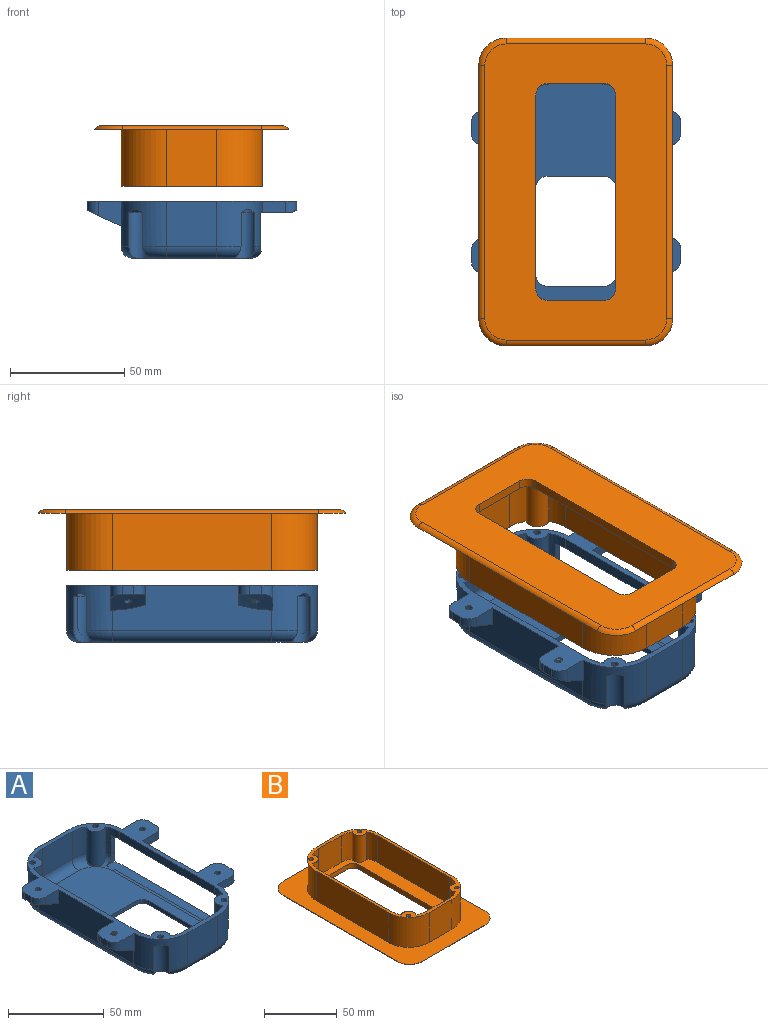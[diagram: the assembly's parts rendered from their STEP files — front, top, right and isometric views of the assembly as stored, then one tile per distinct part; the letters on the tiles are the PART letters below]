
ASSEMBLY  parts=2 mates=1
PART A: 110 faces, bbox 92.7x114x26.4 mm
  f0: cylinder r=20mm len=20mm, axis (0,0,1), area 413.3mm2, adj f12,f23,f36,f37,f71,f72,f96,f101
  f1: cylinder r=20mm len=20mm, axis (0,0,-1), area 421.8mm2, adj f6,f21,f36,f38,f75,f76,f93,f103
  f2: cylinder r=17.5mm len=17.5mm, axis (0,0,-1), area 84.8mm2, adj f4,f18,f36,f66,f103,f104
  f3: plane 40.6x4.89mm, normal (1,0,0), area 198.5mm2, adj f7,f11,f36,f103
  f4: plane 70x4.89mm, normal (-1,0,0), area 342.3mm2, adj f2,f5,f36,f103
  f5: cylinder r=17.5mm len=17.5mm, axis (0,0,1), area 84.8mm2, adj f4,f20,f36,f64,f101,f102,f103,f106
  f6: plane 10x4.89mm, normal (0,-1,0), area 48.9mm2, adj f1,f9,f36,f103
  f7: plane 10x4.89mm, normal (0,1,0), area 48.9mm2, adj f3,f8,f36,f103
  f8: cylinder r=5mm len=5mm, axis (0,0,-1), area 36.4mm2, adj f7,f16,f36,f45,f103
  f9: cylinder r=5mm len=5mm, axis (0,0,1), area 36.4mm2, adj f6,f16,f36,f45,f103
  f10: cylinder r=1.5mm len=4.89mm, axis (0,0,1), area 46.1mm2, adj f36,f103
  f11: plane 10x4.89mm, normal (0,-1,0), area 48.9mm2, adj f3,f14,f36,f103
  f12: plane 10.03x4.91mm, normal (0,1,0), area 48.9mm2, adj f0,f13,f36,f103
  f13: cylinder r=5mm len=5mm, axis (0,0,-1), area 36.4mm2, adj f12,f17,f36,f46,f103
  f14: cylinder r=5mm len=5mm, axis (0,0,1), area 36.4mm2, adj f11,f17,f36,f46,f103
  f15: cylinder r=1.5mm len=4.89mm, axis (0,0,1), area 46.1mm2, adj f36,f103
  f16: plane 13.28x2.33mm, normal (0.42,0,-0.91), area 22.1mm2, adj f8,f9,f45,f103
  f17: plane 13.28x2.33mm, normal (0.42,0,-0.91), area 22.1mm2, adj f13,f14,f46,f103
  f18: torus R=12.5mm, axis (0,0,1), area 28.9mm2, adj f2,f19,f30,f66,f104,f105
  f19: cylinder r=5mm len=70mm, axis (0,-1,0), area 107.7mm2, adj f18,f20,f30,f105
  f20: torus R=12.5mm, axis (0,0,1), area 28.8mm2, adj f5,f19,f30,f64,f105,f106
  f21: torus R=15mm, axis (0,0,1), area 68.5mm2, adj f1,f22,f31,f76,f104,f105
  f22: cylinder r=5mm len=70mm, axis (0,1,0), area 385.2mm2, adj f21,f23,f31,f105
  f23: torus R=15mm, axis (0,0,1), area 68mm2, adj f0,f22,f31,f72,f105,f106
  f24: cylinder r=20mm len=20mm, axis (0,0,1), area 492.1mm2, adj f35,f36,f38,f56,f62,f73,f74,f88
  f25: cylinder r=20mm len=20mm, axis (0,0,-1), area 491.2mm2, adj f35,f36,f37,f49,f61,f77,f78,f90
  f26: cylinder r=1.5mm len=3.37mm, axis (0,0,1), area 30.7mm2, adj f36,f77
  f27: cylinder r=1.5mm len=3.23mm, axis (0,0,1), area 29.7mm2, adj f36,f75
  f28: cylinder r=1.5mm len=3.21mm, axis (0,0,1), area 29.7mm2, adj f36,f73
  f29: cylinder r=1.5mm len=3.35mm, axis (0,0,1), area 31mm2, adj f36,f71
  f30: plane 95x47mm, normal (0,0,1), area 2659mm2, adj f18,f19,f20,f67,f68,f69,f70,f79
  f31: plane 100x52mm, normal (0,0,-1), area 3304.1mm2, adj f21,f22,f23,f67,f68,f69,f70,f72
  f32: cylinder r=17.5mm len=17.5mm, axis (0,0,1), area 152.7mm2, adj f36,f41,f65,f79
  f33: cylinder r=17.5mm len=17.5mm, axis (0,0,1), area 152.7mm2, adj f36,f39,f64,f87
  f34: cylinder r=17.5mm len=17.5mm, axis (0,0,-1), area 152.7mm2, adj f36,f40,f63,f84
  f35: plane 70x20mm, normal (-1,0,0), area 1103.1mm2, adj f24,f25,f36,f47,f54,f61,f62,f89
  f36: plane 110.24x92.04mm, normal (0,0,1), area 1695.1mm2, adj f0,f1,f2,f3,f4,f5,f6,f7
  f37: plane 22x20mm, normal (0,1,0), area 440mm2, adj f0,f25,f36,f95
  f38: plane 22x20mm, normal (0,-1,0), area 440mm2, adj f1,f24,f36,f92
  f39: plane 22x17.5mm, normal (0,-1,0), area 385mm2, adj f33,f36,f42,f86
  f40: plane 70x17.5mm, normal (1,0,0), area 1225mm2, adj f34,f36,f43,f83
  f41: plane 22x17.5mm, normal (0,1,0), area 385mm2, adj f32,f36,f44,f80
  f42: cylinder r=17.5mm len=17.5mm, axis (0,0,-1), area 152.7mm2, adj f36,f39,f63,f85
  f43: cylinder r=17.5mm len=17.5mm, axis (0,0,1), area 152.7mm2, adj f36,f40,f65,f82
  f44: cylinder r=17.5mm len=17.5mm, axis (0,0,-1), area 152.7mm2, adj f36,f41,f66,f81
  f45: plane 5x4mm, normal (1,0,0), area 20mm2, adj f8,f9,f16,f36
  f46: plane 5x4mm, normal (1,0,0), area 20mm2, adj f13,f14,f17,f36
  f47: plane 9.8x8.83mm, normal (0,-1,0), area 67.6mm2, adj f35,f36,f51,f61
  f48: plane 9.87x2.64mm, normal (0,0,-1), area 7.2mm2, adj f50,f51,f52,f61
  f49: plane 11.05x9.86mm, normal (0,1,0), area 85.5mm2, adj f25,f36,f52,f61
  f50: plane 5x4mm, normal (-1,0,0), area 20mm2, adj f36,f48,f51,f52
  f51: cylinder r=5mm len=5mm, axis (0,0,-1), area 32.5mm2, adj f36,f47,f48,f50,f61
  f52: cylinder r=5mm len=6.42mm, axis (0,0,1), area 38.6mm2, adj f36,f48,f49,f50,f61
  f53: cylinder r=1.5mm len=7.61mm, axis (0,0,1), area 66.6mm2, adj f36,f61
  f54: plane 9.8x8.78mm, normal (0,1,0), area 67.1mm2, adj f35,f36,f59,f62
  f55: plane 10.04x2.75mm, normal (0,0,-1), area 7.8mm2, adj f57,f58,f59,f62
  f56: plane 11.03x9.84mm, normal (0,-1,0), area 85.4mm2, adj f24,f36,f58,f62
  f57: plane 5x4mm, normal (-1,0,0), area 20mm2, adj f36,f55,f58,f59
  f58: cylinder r=5mm len=6.43mm, axis (0,0,-1), area 38.6mm2, adj f36,f55,f56,f57,f62
  f59: cylinder r=5mm len=5mm, axis (0,0,1), area 32.4mm2, adj f36,f54,f55,f57,f62
  f60: cylinder r=1.5mm len=7.87mm, axis (0,0,1), area 36.8mm2, adj f36,f62,f107,f108,f109
  f61: cone r=20mm half-angle=65deg, axis (0,0,1), area 217.3mm2, adj f25,f35,f47,f48,f49,f51,f52,f53
  f62: cone r=20mm half-angle=65deg, axis (0,0,1), area 215.7mm2, adj f24,f35,f54,f55,f56,f58,f59,f60
  f63: cylinder r=5mm len=22.5mm, axis (0,0,-1), area 285.5mm2, adj f34,f36,f42,f84,f85
  f64: cylinder r=5mm len=22.5mm, axis (0,0,-1), area 285.5mm2, adj f5,f20,f33,f36,f87
  f65: cylinder r=5mm len=22.5mm, axis (0,0,-1), area 285.5mm2, adj f32,f36,f43,f79,f82
  f66: cylinder r=5mm len=22.5mm, axis (0,0,-1), area 285.5mm2, adj f2,f18,f36,f44,f81
  f67: plane 25.14x2.5mm, normal (0,1,0), area 62.8mm2, adj f30,f31,f97,f100
  f68: plane 38.19x2.5mm, normal (1,0,0), area 95.5mm2, adj f30,f31,f97,f98
  f69: plane 25.14x2.5mm, normal (0,-1,0), area 62.8mm2, adj f30,f31,f98,f99
  f70: plane 38.19x2.5mm, normal (-1,0,0), area 95.5mm2, adj f30,f31,f99,f100
  f71: cone r=0mm half-angle=59deg, axis (0,0,-1), area 48.6mm2, adj f0,f29,f72
  f72: cylinder r=4.5mm len=20mm, axis (0,0,-1), area 332.2mm2, adj f0,f23,f31,f71,f96
  f73: cone r=0mm half-angle=59deg, axis (0,0,-1), area 51.3mm2, adj f24,f28,f74
  f74: cylinder r=4.5mm len=20mm, axis (0,0,-1), area 329.3mm2, adj f24,f31,f73,f88,f91
  f75: cone r=0mm half-angle=59deg, axis (0,0,-1), area 50.2mm2, adj f1,f27,f76
  f76: cylinder r=4.5mm len=20mm, axis (0,0,-1), area 327.8mm2, adj f1,f21,f31,f75,f93
  f77: cone r=0mm half-angle=59deg, axis (0,0,-1), area 49.4mm2, adj f25,f26,f78
  f78: cylinder r=4.5mm len=20mm, axis (0,0,-1), area 333.2mm2, adj f25,f31,f77,f90,f94
  f79: torus R=12.5mm, axis (0,0,1), area 64.5mm2, adj f30,f32,f65,f80
  f80: cylinder r=5mm len=22mm, axis (-1,0,0), area 172.8mm2, adj f30,f41,f79,f81
  f81: torus R=12.5mm, axis (0,0,1), area 64.5mm2, adj f30,f44,f66,f80
  f82: torus R=12.5mm, axis (0,0,1), area 64.5mm2, adj f30,f43,f65,f83
  f83: cylinder r=5mm len=70mm, axis (0,1,0), area 549.8mm2, adj f30,f40,f82,f84
  f84: torus R=12.5mm, axis (0,0,1), area 64.5mm2, adj f30,f34,f63,f83
  f85: torus R=12.5mm, axis (0,0,1), area 64.5mm2, adj f30,f42,f63,f86
  f86: cylinder r=5mm len=22mm, axis (1,0,0), area 172.8mm2, adj f30,f39,f85,f87
  f87: torus R=12.5mm, axis (0,0,1), area 64.5mm2, adj f30,f33,f64,f86
  f88: torus R=15mm, axis (0,0,1), area 81.5mm2, adj f24,f31,f74,f89
  f89: cylinder r=5mm len=70mm, axis (0,-1,0), area 549.8mm2, adj f31,f35,f88,f90
  f90: torus R=15mm, axis (0,0,1), area 80.9mm2, adj f25,f31,f78,f89
  f91: torus R=15mm, axis (0,0,1), area 76mm2, adj f24,f31,f74,f92
  f92: cylinder r=5mm len=22mm, axis (1,0,0), area 172.8mm2, adj f31,f38,f91,f93
  f93: torus R=15mm, axis (0,0,1), area 76.3mm2, adj f1,f31,f76,f92
  f94: torus R=15mm, axis (0,0,1), area 76.5mm2, adj f25,f31,f78,f95
  f95: cylinder r=5mm len=22mm, axis (-1,0,0), area 172.8mm2, adj f31,f37,f94,f96
  f96: torus R=15mm, axis (0,0,1), area 76.7mm2, adj f0,f31,f72,f95
  f97: cylinder r=5mm len=5mm, axis (0,0,1), area 19.6mm2, adj f30,f31,f67,f68
  f98: cylinder r=5mm len=5mm, axis (0,0,1), area 19.6mm2, adj f30,f31,f68,f69
  f99: cylinder r=5mm len=5mm, axis (0,0,-1), area 19.6mm2, adj f30,f31,f69,f70
  f100: cylinder r=5mm len=5mm, axis (0,0,-1), area 19.6mm2, adj f30,f31,f67,f70
  f101: plane 2.61x0.01mm, normal (0,0,-1), area 0mm2, adj f0,f5,f102,f106
  f102: plane 11.98x2.61mm, normal (0,-1,0), area 31.2mm2, adj f0,f5,f101,f103
  f103: plane 80.61x16.42mm, normal (0,0,-1), area 576.3mm2, adj f0,f1,f2,f3,f4,f5,f6,f7
  f104: plane 18.08x7.02mm, normal (0,1,0), area 49.6mm2, adj f1,f2,f18,f21,f103,f105
  f105: plane 80.62x6.49mm, normal (0,0,1), area 439.9mm2, adj f18,f19,f20,f21,f22,f23,f104,f106
  f106: plane 7.02x6.1mm, normal (0,-1,0), area 18.3mm2, adj f0,f5,f20,f23,f101,f105
  f107: plane 0.92x0.61mm, normal (0,1,0), area 0.3mm2, adj f60,f108,f109
  f108: bspline ~7.75x4.87mm, area 31.3mm2, adj f36,f60,f107,f109
  f109: bspline ~7.97x4.87mm, area 29.9mm2, adj f36,f60,f62,f107,f108
PART B: 52 faces, bbox 87.8x137.8x26.5 mm
  f0: plane 105x57mm, normal (0,0,1), area 2271mm2, adj f2,f3,f4,f5,f15,f16,f17,f18
  f1: plane 129.8x79.8mm, normal (0,0,-1), area 6979.4mm2, adj f36,f37,f38,f39,f40,f41,f42,f43
  f2: cylinder r=17.5mm len=22.5mm, axis (0,0,-1), area 196.4mm2, adj f0,f6,f15,f26
  f3: cylinder r=17.5mm len=22.5mm, axis (0,0,1), area 196.4mm2, adj f0,f6,f18,f25
  f4: cylinder r=17.5mm len=22.5mm, axis (0,0,1), area 196.4mm2, adj f0,f6,f16,f24
  f5: cylinder r=17.5mm len=22.5mm, axis (0,0,-1), area 196.4mm2, adj f0,f6,f17,f23
  f6: plane 110x62mm, normal (0,0,1), area 873.8mm2, adj f2,f3,f4,f5,f7,f8,f9,f10
  f7: plane 70x25mm, normal (1,0,0), area 1750mm2, adj f6,f11,f14,f35
  f8: plane 25x22mm, normal (0,1,0), area 550mm2, adj f6,f11,f12,f35
  f9: plane 70x25mm, normal (-1,0,0), area 1750mm2, adj f6,f12,f13,f35
  f10: plane 25x22mm, normal (0,-1,0), area 550mm2, adj f6,f13,f14,f35
  f11: cylinder r=20mm len=25mm, axis (0,0,1), area 785.4mm2, adj f6,f7,f8,f35
  f12: cylinder r=20mm len=25mm, axis (0,0,-1), area 785.4mm2, adj f6,f8,f9,f35
  f13: cylinder r=20mm len=25mm, axis (0,0,1), area 785.4mm2, adj f6,f9,f10,f35
  f14: cylinder r=20mm len=25mm, axis (0,0,-1), area 785.4mm2, adj f6,f7,f10,f35
  f15: plane 70x22.5mm, normal (-1,0,0), area 1575mm2, adj f0,f2,f6,f19
  f16: plane 22.5x22mm, normal (0,-1,0), area 495mm2, adj f0,f4,f6,f20
  f17: plane 70x22.5mm, normal (1,0,0), area 1575mm2, adj f0,f5,f6,f21
  f18: plane 22.5x22mm, normal (0,1,0), area 495mm2, adj f0,f3,f6,f22
  f19: cylinder r=17.5mm len=22.5mm, axis (0,0,1), area 196.4mm2, adj f0,f6,f15,f24
  f20: cylinder r=17.5mm len=22.5mm, axis (0,0,-1), area 196.4mm2, adj f0,f6,f16,f23
  f21: cylinder r=17.5mm len=22.5mm, axis (0,0,1), area 196.4mm2, adj f0,f6,f17,f25
  f22: cylinder r=17.5mm len=22.5mm, axis (0,0,-1), area 196.4mm2, adj f0,f6,f18,f26
  f23: cylinder r=5mm len=22.5mm, axis (0,0,-1), area 321.2mm2, adj f0,f5,f6,f20
  f24: cylinder r=5mm len=22.5mm, axis (0,0,-1), area 321.2mm2, adj f0,f4,f6,f19
  f25: cylinder r=5mm len=22.5mm, axis (0,0,-1), area 321.2mm2, adj f0,f3,f6,f21
  f26: cylinder r=5mm len=22.5mm, axis (0,0,-1), area 321.2mm2, adj f0,f2,f6,f22
  f27: cone r=0mm half-angle=59deg, axis (0,0,1), area 8.2mm2, adj f28
  f28: cylinder r=1.5mm len=15mm, axis (0,0,1), area 141.4mm2, adj f6,f27
  f29: cone r=0mm half-angle=59deg, axis (0,0,1), area 8.2mm2, adj f30
  f30: cylinder r=1.5mm len=15mm, axis (0,0,1), area 141.4mm2, adj f6,f29
  f31: cone r=0mm half-angle=59deg, axis (0,0,1), area 8.2mm2, adj f32
  f32: cylinder r=1.5mm len=15mm, axis (0,0,1), area 141.4mm2, adj f6,f31
  f33: cone r=0mm half-angle=59deg, axis (0,0,1), area 8.2mm2, adj f34
  f34: cylinder r=1.5mm len=15mm, axis (0,0,1), area 141.4mm2, adj f6,f33
  f35: plane 135x85mm, normal (0,0,1), area 4874.8mm2, adj f7,f8,f9,f10,f11,f12,f13,f14
  f36: plane 85x4mm, normal (1,0,0), area 340mm2, adj f0,f1,f40,f43
  f37: plane 25x4mm, normal (0,-1,0), area 100mm2, adj f0,f1,f40,f41
  f38: plane 85x4mm, normal (-1,0,0), area 340mm2, adj f0,f1,f41,f42
  f39: plane 25x4mm, normal (0,1,0), area 100mm2, adj f0,f1,f42,f43
  f40: cylinder r=5mm len=5mm, axis (0,0,-1), area 31.4mm2, adj f0,f1,f36,f37
  f41: cylinder r=5mm len=5mm, axis (0,0,1), area 31.4mm2, adj f0,f1,f37,f38
  f42: cylinder r=5mm len=5mm, axis (0,0,-1), area 31.4mm2, adj f0,f1,f38,f39
  f43: cylinder r=5mm len=5mm, axis (0,0,1), area 31.4mm2, adj f0,f1,f36,f39
  f44: cylinder r=3mm len=111mm, axis (0,1,0), area 348.7mm2, adj f1,f35,f45,f46
  f45: torus R=9.4mm, axis (0,0,-1), area 53.5mm2, adj f1,f35,f44,f47
  f46: torus R=9.4mm, axis (0,0,-1), area 53.5mm2, adj f1,f35,f44,f48
  f47: cylinder r=3mm len=61mm, axis (-1,0,0), area 191.6mm2, adj f1,f35,f45,f49
  f48: cylinder r=3mm len=61mm, axis (-1,0,0), area 191.6mm2, adj f1,f35,f46,f50
  f49: torus R=9.4mm, axis (0,0,-1), area 53.5mm2, adj f1,f35,f47,f51
  f50: torus R=9.4mm, axis (0,0,-1), area 53.5mm2, adj f1,f35,f48,f51
  f51: cylinder r=3mm len=111mm, axis (0,1,0), area 348.7mm2, adj f1,f35,f49,f50
PLACE A rot(axis=(0,0,-1),0deg) t=(-34.16,3.39,-8.14)mm
PLACE B rot(axis=(0,-1,0),180deg) t=(-34.16,3.39,48.32)mm
MATE slider B.f24 <-> A.f26  axis (0,0,-1) through (-57.53,50.77,23.32)mm
